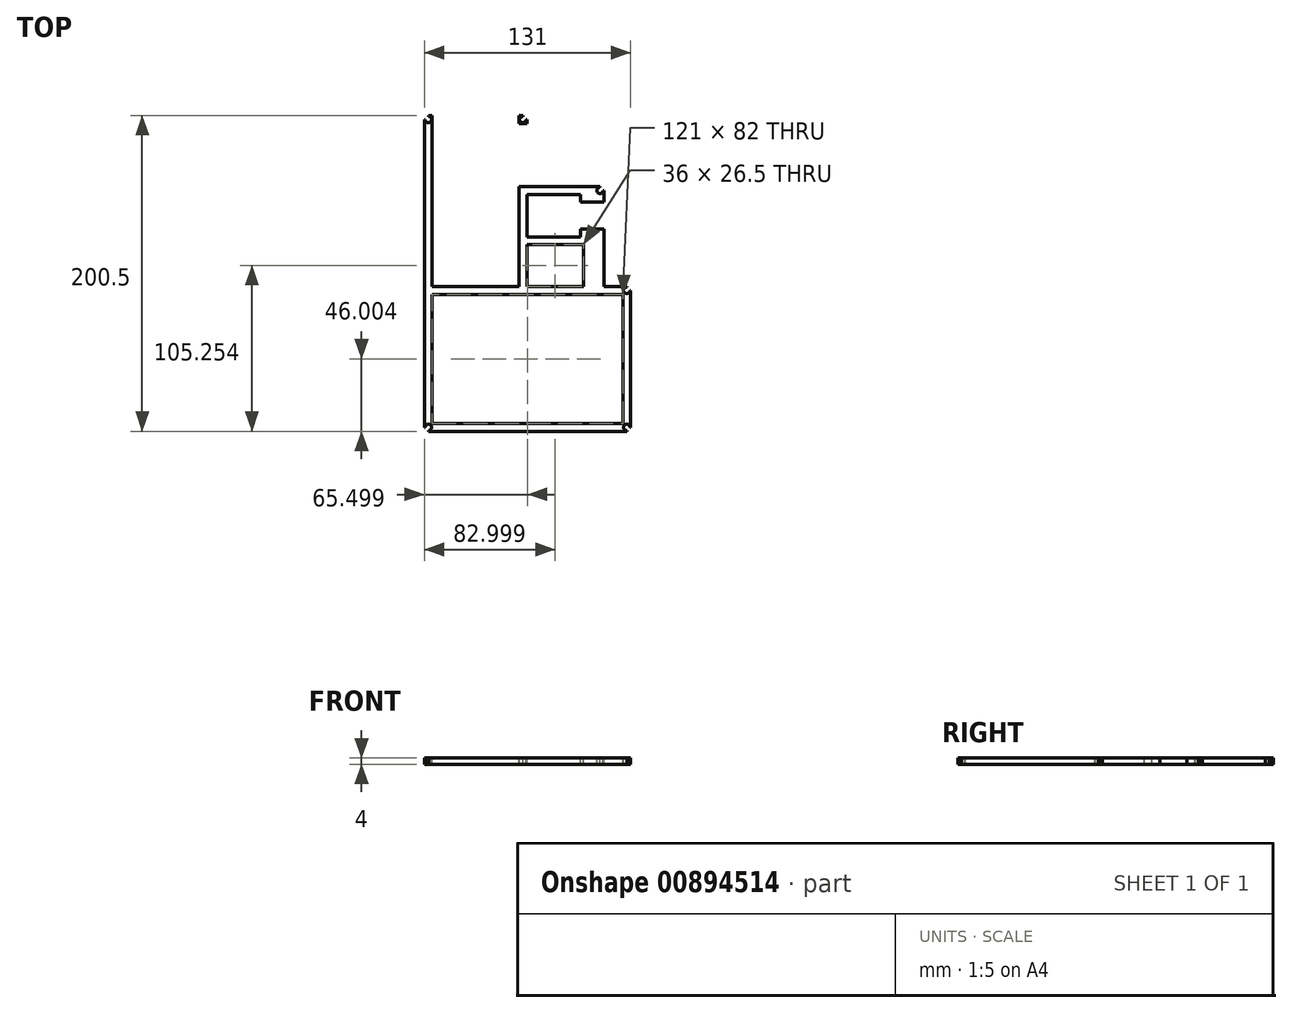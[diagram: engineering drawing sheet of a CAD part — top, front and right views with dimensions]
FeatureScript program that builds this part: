
annotation { "Feature Type Name" : "Feature", "Feature Type Description" : "" }
export const myFeature = defineFeature(function(context is Context, id is Id, definition is map)
    precondition{}
    {
        {
            var Q0;
            Q0=qCreatedBy(makeId("Top.planeOp"),FACE);
            var sketch = newSketch(context, id + "F0", { "sketchPlane" : qUnion([Q0])});
            skLineSegment(sketch, "E0.bottom", {"start": v(-40.7, -58.83) * mm, "end": v(14.3, -58.83) * mm});
            skLineSegment(sketch, "E0.top", {"start": v(-40.7, 44.67) * mm, "end": v(14.3, 44.67) * mm});
            skLineSegment(sketch, "E0.left", {"start": v(-40.7, -58.83) * mm, "end": v(-40.7, 44.67) * mm});
            skLineSegment(sketch, "E0.right", {"start": v(14.3, -58.83) * mm, "end": v(14.3, 44.67) * mm});
            skLineSegment(sketch, "E1.bottom", {"start": v(-45.7, 49.67) * mm, "end": v(85.3, 49.67) * mm});
            skLineSegment(sketch, "E1.top", {"start": v(-45.7, -150.83) * mm, "end": v(85.3, -150.83) * mm});
            skLineSegment(sketch, "E1.left", {"start": v(-45.7, 49.67) * mm, "end": v(-45.7, -150.83) * mm});
            skLineSegment(sketch, "E1.right", {"start": v(85.3, 49.67) * mm, "end": v(85.3, -150.83) * mm});
            skLineSegment(sketch, "E2.bottom", {"start": v(-40.7, -63.83) * mm, "end": v(80.3, -63.83) * mm});
            skLineSegment(sketch, "E2.top", {"start": v(-40.7, -145.83) * mm, "end": v(80.3, -145.83) * mm});
            skLineSegment(sketch, "E2.left", {"start": v(-40.7, -63.83) * mm, "end": v(-40.7, -145.83) * mm});
            skLineSegment(sketch, "E2.right", {"start": v(80.3, -63.83) * mm, "end": v(80.3, -145.83) * mm});
            skLineSegment(sketch, "E3.top", {"start": v(14.3, -63.83) * mm, "end": v(19.3, -63.83) * mm});
            skLineSegment(sketch, "E4.bottom", {"start": v(19.3, -58.83) * mm, "end": v(55.3, -58.83) * mm});
            skLineSegment(sketch, "E4.top", {"start": v(19.3, -32.33) * mm, "end": v(55.3, -32.33) * mm});
            skLineSegment(sketch, "E4.left", {"start": v(19.3, -58.83) * mm, "end": v(19.3, -32.33) * mm});
            skLineSegment(sketch, "E4.right", {"start": v(55.3, -58.83) * mm, "end": v(55.3, -32.33) * mm});
            skLineSegment(sketch, "E5.right", {"start": v(14.3, -32.33) * mm, "end": v(14.3, -27.33) * mm});
            skLineSegment(sketch, "E6.bottom", {"start": v(19.3, -27.33) * mm, "end": v(53.3, -27.33) * mm});
            skLineSegment(sketch, "E6.top", {"start": v(19.3, -0.33) * mm, "end": v(53.3, -0.33) * mm});
            skLineSegment(sketch, "E6.left", {"start": v(19.3, -27.33) * mm, "end": v(19.3, -0.33) * mm});
            skLineSegment(sketch, "E6.right", {"start": v(53.3, -27.33) * mm, "end": v(53.3, -0.33) * mm});
            skLineSegment(sketch, "E7", {"start": v(53.3, -27.33) * mm, "end": v(53.3, -22.33) * mm});
            skLineSegment(sketch, "E8", {"start": v(53.3, -22.33) * mm, "end": v(53.3, -5.33) * mm});
            skLineSegment(sketch, "E9.bottom", {"start": v(53.3, -5.33) * mm, "end": v(53.3, -5.33) * mm});
            skLineSegment(sketch, "E9.top", {"start": v(53.3, -22.33) * mm, "end": v(53.3, -22.33) * mm});
            skLineSegment(sketch, "E9.left", {"start": v(53.3, -5.33) * mm, "end": v(53.3, -22.33) * mm});
            skLineSegment(sketch, "E9.right", {"start": v(53.3, -5.33) * mm, "end": v(53.3, -22.33) * mm});
            skLineSegment(sketch, "E10.bottom", {"start": v(53.3, -22.33) * mm, "end": v(63.3, -22.33) * mm});
            skLineSegment(sketch, "E10.top", {"start": v(53.3, -5.33) * mm, "end": v(63.3, -5.33) * mm});
            skLineSegment(sketch, "E10.right", {"start": v(63.3, -22.33) * mm, "end": v(63.3, -5.33) * mm});
            skLineSegment(sketch, "E11.bottom", {"start": v(14.3, 44.67) * mm, "end": v(19.3, 44.67) * mm});
            skLineSegment(sketch, "E11.top", {"start": v(14.3, 49.67) * mm, "end": v(19.3, 49.67) * mm});
            skLineSegment(sketch, "E11.left", {"start": v(14.3, 44.67) * mm, "end": v(14.3, 49.67) * mm});
            skLineSegment(sketch, "E11.right", {"start": v(19.3, 44.67) * mm, "end": v(19.3, 49.67) * mm});
            skLineSegment(sketch, "E12.bottom", {"start": v(19.3, -0.33) * mm, "end": v(14.3, -0.33) * mm});
            skLineSegment(sketch, "E12.top", {"start": v(19.3, 4.67) * mm, "end": v(14.3, 4.67) * mm});
            skLineSegment(sketch, "E12.left", {"start": v(19.3, -0.33) * mm, "end": v(19.3, 4.67) * mm});
            skLineSegment(sketch, "E12.right", {"start": v(14.3, -0.33) * mm, "end": v(14.3, 4.67) * mm});
            skLineSegment(sketch, "E13.bottom", {"start": v(85.3, 49.67) * mm, "end": v(80.3, 49.67) * mm});
            skLineSegment(sketch, "E13.left", {"start": v(85.3, 49.67) * mm, "end": v(85.3, 44.67) * mm});
            skLineSegment(sketch, "E14.top", {"start": v(19.3, 49.67) * mm, "end": v(85.3, 49.67) * mm});
            skLineSegment(sketch, "E14.left", {"start": v(19.3, 4.67) * mm, "end": v(19.3, 49.67) * mm});
            skLineSegment(sketch, "E14.right", {"start": v(85.3, 4.67) * mm, "end": v(85.3, 49.67) * mm});
            skLineSegment(sketch, "E15.bottom", {"start": v(80.3, -63.83) * mm, "end": v(85.3, -63.83) * mm});
            skLineSegment(sketch, "E15.top", {"start": v(80.3, -58.83) * mm, "end": v(85.3, -58.83) * mm});
            skLineSegment(sketch, "E15.left", {"start": v(80.3, -63.83) * mm, "end": v(80.3, -58.83) * mm});
            skLineSegment(sketch, "E15.right", {"start": v(85.3, -63.83) * mm, "end": v(85.3, -58.83) * mm});
            skLineSegment(sketch, "E16", {"start": v(63.3, -5.33) * mm, "end": v(68.3, -5.33) * mm});
            skLineSegment(sketch, "E17", {"start": v(68.3, -5.33) * mm, "end": v(68.3, -22.33) * mm});
            skLineSegment(sketch, "E18.bottom", {"start": v(85.3, -58.83) * mm, "end": v(68.3, -58.83) * mm});
            skLineSegment(sketch, "E18.left", {"start": v(85.3, -58.83) * mm, "end": v(85.3, 4.67) * mm});
            skLineSegment(sketch, "E18.right", {"start": v(68.3, -58.83) * mm, "end": v(68.3, 4.67) * mm});
            skLineSegment(sketch, "E19", {"start": v(19.3, 4.67) * mm, "end": v(68.3, 4.67) * mm});
            skLineSegment(sketch, "E20.bottom", {"start": v(68.3, 4.67) * mm, "end": v(65.8, 4.67) * mm});
            skLineSegment(sketch, "E20.top", {"start": v(68.3, 2.17) * mm, "end": v(65.8, 2.17) * mm});
            skLineSegment(sketch, "E20.left", {"start": v(68.3, 4.67) * mm, "end": v(68.3, 2.17) * mm});
            skLineSegment(sketch, "E20.right", {"start": v(65.8, 4.67) * mm, "end": v(65.8, 2.17) * mm});
            skLineSegment(sketch, "E21.bottom", {"start": v(19.3, 44.67) * mm, "end": v(16.8, 44.67) * mm});
            skLineSegment(sketch, "E21.top", {"start": v(19.3, 47.17) * mm, "end": v(16.8, 47.17) * mm});
            skLineSegment(sketch, "E21.left", {"start": v(19.3, 44.67) * mm, "end": v(19.3, 47.17) * mm});
            skLineSegment(sketch, "E22.bottom", {"start": v(85.3, -58.83) * mm, "end": v(82.8, -58.83) * mm});
            skLineSegment(sketch, "E22.top", {"start": v(85.3, -61.33) * mm, "end": v(82.8, -61.33) * mm});
            skLineSegment(sketch, "E22.left", {"start": v(85.3, -58.83) * mm, "end": v(85.3, -61.33) * mm});
            skLineSegment(sketch, "E22.right", {"start": v(82.8, -58.83) * mm, "end": v(82.8, -61.33) * mm});
            skLineSegment(sketch, "E23.bottom", {"start": v(85.3, -150.83) * mm, "end": v(82.8, -150.83) * mm});
            skLineSegment(sketch, "E23.top", {"start": v(85.3, -148.33) * mm, "end": v(82.8, -148.33) * mm});
            skLineSegment(sketch, "E23.left", {"start": v(85.3, -150.83) * mm, "end": v(85.3, -148.33) * mm});
            skLineSegment(sketch, "E23.right", {"start": v(82.8, -150.83) * mm, "end": v(82.8, -148.33) * mm});
            skLineSegment(sketch, "E24.bottom", {"start": v(-45.7, -150.83) * mm, "end": v(-43.2, -150.83) * mm});
            skLineSegment(sketch, "E24.top", {"start": v(-45.7, -148.33) * mm, "end": v(-43.2, -148.33) * mm});
            skLineSegment(sketch, "E24.left", {"start": v(-45.7, -150.83) * mm, "end": v(-45.7, -148.33) * mm});
            skLineSegment(sketch, "E24.right", {"start": v(-43.2, -150.83) * mm, "end": v(-43.2, -148.33) * mm});
            skLineSegment(sketch, "E25.bottom", {"start": v(-45.7, 49.67) * mm, "end": v(-43.2, 49.67) * mm});
            skLineSegment(sketch, "E25.top", {"start": v(-45.7, 47.17) * mm, "end": v(-43.2, 47.17) * mm});
            skLineSegment(sketch, "E25.left", {"start": v(-45.7, 49.67) * mm, "end": v(-45.7, 47.17) * mm});
            skLineSegment(sketch, "E25.right", {"start": v(-43.2, 49.67) * mm, "end": v(-43.2, 47.17) * mm});
            skLineSegment(sketch, "E26.bottom", {"start": v(19.3, 49.67) * mm, "end": v(16.8, 49.67) * mm});
            skLineSegment(sketch, "E26.left", {"start": v(19.3, 49.67) * mm, "end": v(19.3, 47.17) * mm});
            skLineSegment(sketch, "E26.right", {"start": v(16.8, 49.67) * mm, "end": v(16.8, 47.17) * mm});
            skCircle(sketch, "E27", {"center": v(16.8, 47.17) * mm, "radius": 2 * mm});
            skCircle(sketch, "E28", {"center": v(65.8, 2.17) * mm, "radius": 2 * mm});
            skCircle(sketch, "E29", {"center": v(82.8, -61.33) * mm, "radius": 2 * mm});
            skCircle(sketch, "E30", {"center": v(82.8, -148.33) * mm, "radius": 2 * mm});
            skCircle(sketch, "E31", {"center": v(-43.2, -148.33) * mm, "radius": 2 * mm});
            skCircle(sketch, "E32", {"center": v(-43.2, 47.17) * mm, "radius": 2 * mm});
            skLineSegment(sketch, "E33.bottom", {"start": v(-40.7, -63.83) * mm, "end": v(-37.3, -63.83) * mm});
            skLineSegment(sketch, "E33.top", {"start": v(-40.7, -67.23) * mm, "end": v(-37.3, -67.23) * mm});
            skLineSegment(sketch, "E33.left", {"start": v(-40.7, -63.83) * mm, "end": v(-40.7, -67.23) * mm});
            skLineSegment(sketch, "E33.right", {"start": v(-37.3, -63.83) * mm, "end": v(-37.3, -67.23) * mm});
            skLineSegment(sketch, "E34.bottom", {"start": v(-40.7, -145.83) * mm, "end": v(-37.3, -145.83) * mm});
            skLineSegment(sketch, "E34.top", {"start": v(-40.7, -142.43) * mm, "end": v(-37.3, -142.43) * mm});
            skLineSegment(sketch, "E34.left", {"start": v(-40.7, -145.83) * mm, "end": v(-40.7, -142.43) * mm});
            skLineSegment(sketch, "E34.right", {"start": v(-37.3, -145.83) * mm, "end": v(-37.3, -142.43) * mm});
            skLineSegment(sketch, "E35.bottom", {"start": v(80.3, -145.83) * mm, "end": v(76.9, -145.83) * mm});
            skLineSegment(sketch, "E35.top", {"start": v(80.3, -142.43) * mm, "end": v(76.9, -142.43) * mm});
            skLineSegment(sketch, "E35.left", {"start": v(80.3, -145.83) * mm, "end": v(80.3, -142.43) * mm});
            skLineSegment(sketch, "E35.right", {"start": v(76.9, -145.83) * mm, "end": v(76.9, -142.43) * mm});
            skLineSegment(sketch, "E36.bottom", {"start": v(80.3, -63.83) * mm, "end": v(76.9, -63.83) * mm});
            skLineSegment(sketch, "E36.top", {"start": v(80.3, -67.23) * mm, "end": v(76.9, -67.23) * mm});
            skLineSegment(sketch, "E36.left", {"start": v(80.3, -63.83) * mm, "end": v(80.3, -67.23) * mm});
            skLineSegment(sketch, "E36.right", {"start": v(76.9, -63.83) * mm, "end": v(76.9, -67.23) * mm});
            skLineSegment(sketch, "E37.bottom", {"start": v(-40.7, -58.83) * mm, "end": v(-37.7, -58.83) * mm});
            skLineSegment(sketch, "E37.top", {"start": v(-40.7, 28.47) * mm, "end": v(-37.7, 28.47) * mm});
            skLineSegment(sketch, "E37.left", {"start": v(-40.7, -58.83) * mm, "end": v(-40.7, 28.47) * mm});
            skLineSegment(sketch, "E37.right", {"start": v(-37.7, -58.83) * mm, "end": v(-37.7, 28.47) * mm});
            skLineSegment(sketch, "E38.bottom", {"start": v(-37.7, -58.83) * mm, "end": v(-40.7, -58.83) * mm});
            skLineSegment(sketch, "E38.top", {"start": v(-37.7, -52.83) * mm, "end": v(-40.7, -52.83) * mm});
            skLineSegment(sketch, "E38.left", {"start": v(-37.7, -58.83) * mm, "end": v(-37.7, -52.83) * mm});
            skLineSegment(sketch, "E38.right", {"start": v(-40.7, -58.83) * mm, "end": v(-40.7, -52.83) * mm});
            skLineSegment(sketch, "E39.bottom", {"start": v(14.3, -58.83) * mm, "end": v(11.3, -58.83) * mm});
            skLineSegment(sketch, "E39.top", {"start": v(14.3, 29.87) * mm, "end": v(11.3, 29.87) * mm});
            skLineSegment(sketch, "E39.left", {"start": v(14.3, -58.83) * mm, "end": v(14.3, 29.87) * mm});
            skLineSegment(sketch, "E39.right", {"start": v(11.3, -58.83) * mm, "end": v(11.3, 29.87) * mm});
            skLineSegment(sketch, "E40.top", {"start": v(14.3, -47.23) * mm, "end": v(11.3, -47.23) * mm});
            skLineSegment(sketch, "E40.left", {"start": v(14.3, -58.83) * mm, "end": v(14.3, -47.23) * mm});
            skLineSegment(sketch, "E40.right", {"start": v(11.3, -58.83) * mm, "end": v(11.3, -47.23) * mm});
            skCircle(sketch, "E41", {"center": v(-37.7, -52.83) * mm, "radius": 2 * mm});
            skCircle(sketch, "E42", {"center": v(-37.7, 28.47) * mm, "radius": 2 * mm});
            skCircle(sketch, "E43", {"center": v(11.3, 29.87) * mm, "radius": 2 * mm});
            skCircle(sketch, "E44", {"center": v(11.3, -47.23) * mm, "radius": 2 * mm});
            skLineSegment(sketch, "E45.bottom", {"start": v(19.3, -0.33) * mm, "end": v(28.55, -0.33) * mm});
            skLineSegment(sketch, "E45.top", {"start": v(19.3, -2.28) * mm, "end": v(28.55, -2.28) * mm});
            skLineSegment(sketch, "E45.left", {"start": v(19.3, -0.33) * mm, "end": v(19.3, -2.28) * mm});
            skLineSegment(sketch, "E45.right", {"start": v(28.55, -0.33) * mm, "end": v(28.55, -2.28) * mm});
            skLineSegment(sketch, "E46.bottom", {"start": v(19.3, -27.33) * mm, "end": v(28.55, -27.33) * mm});
            skLineSegment(sketch, "E46.top", {"start": v(19.3, -25.38) * mm, "end": v(28.55, -25.38) * mm});
            skLineSegment(sketch, "E46.left", {"start": v(19.3, -27.33) * mm, "end": v(19.3, -25.38) * mm});
            skLineSegment(sketch, "E46.right", {"start": v(28.55, -27.33) * mm, "end": v(28.55, -25.38) * mm});
            skLineSegment(sketch, "E47.bottom", {"start": v(53.3, -0.33) * mm, "end": v(51.35, -0.33) * mm});
            skLineSegment(sketch, "E47.top", {"start": v(53.3, -2.28) * mm, "end": v(51.35, -2.28) * mm});
            skLineSegment(sketch, "E47.left", {"start": v(53.3, -0.33) * mm, "end": v(53.3, -2.28) * mm});
            skLineSegment(sketch, "E47.right", {"start": v(51.35, -0.33) * mm, "end": v(51.35, -2.28) * mm});
            skLineSegment(sketch, "E48.bottom", {"start": v(53.3, -27.33) * mm, "end": v(51.35, -27.33) * mm});
            skLineSegment(sketch, "E48.top", {"start": v(53.3, -25.38) * mm, "end": v(51.35, -25.38) * mm});
            skLineSegment(sketch, "E48.left", {"start": v(53.3, -27.33) * mm, "end": v(53.3, -25.38) * mm});
            skLineSegment(sketch, "E48.right", {"start": v(51.35, -27.33) * mm, "end": v(51.35, -25.38) * mm});
            skLineSegment(sketch, "E49.bottom", {"start": v(55.3, -32.33) * mm, "end": v(53.6, -32.33) * mm});
            skLineSegment(sketch, "E49.top", {"start": v(55.3, -34.03) * mm, "end": v(53.6, -34.03) * mm});
            skLineSegment(sketch, "E49.left", {"start": v(55.3, -32.33) * mm, "end": v(55.3, -34.03) * mm});
            skLineSegment(sketch, "E49.right", {"start": v(53.6, -32.33) * mm, "end": v(53.6, -34.03) * mm});
            skLineSegment(sketch, "E50.bottom", {"start": v(55.3, -58.83) * mm, "end": v(53.6, -58.83) * mm});
            skLineSegment(sketch, "E50.top", {"start": v(55.3, -57.13) * mm, "end": v(53.6, -57.13) * mm});
            skLineSegment(sketch, "E50.left", {"start": v(55.3, -58.83) * mm, "end": v(55.3, -57.13) * mm});
            skLineSegment(sketch, "E50.right", {"start": v(53.6, -58.83) * mm, "end": v(53.6, -57.13) * mm});
            skCircle(sketch, "E51", {"center": v(53.6, -34.03) * mm, "radius": 1.2 * mm});
            skCircle(sketch, "E52", {"center": v(53.6, -57.13) * mm, "radius": 1.2 * mm});
            skCircle(sketch, "E53", {"center": v(51.35, -25.38) * mm, "radius": 1.15 * mm});
            skCircle(sketch, "E54", {"center": v(28.55, -25.38) * mm, "radius": 1.15 * mm});
            skCircle(sketch, "E55", {"center": v(28.55, -2.28) * mm, "radius": 1.15 * mm});
            skCircle(sketch, "E56", {"center": v(51.35, -2.28) * mm, "radius": 1.15 * mm});
            skCircle(sketch, "E57", {"center": v(-37.3, -67.23) * mm, "radius": 1.4 * mm});
            skCircle(sketch, "E58", {"center": v(76.9, -67.23) * mm, "radius": 1.4 * mm});
            skCircle(sketch, "E59", {"center": v(-37.3, -142.43) * mm, "radius": 1.4 * mm});
            skCircle(sketch, "E60", {"center": v(76.9, -142.43) * mm, "radius": 1.4 * mm});
            skLineSegment(sketch, "E61", {"start": v(68.3, -22.33) * mm, "end": v(63.3, -22.33) * mm});
            skLineSegment(sketch, "E62.bottom", {"start": v(-40.7, 44.67) * mm, "end": v(-35.7, 44.67) * mm});
            skLineSegment(sketch, "E62.top", {"start": v(-40.7, 49.67) * mm, "end": v(-35.7, 49.67) * mm});
            skLineSegment(sketch, "E62.left", {"start": v(-40.7, 44.67) * mm, "end": v(-40.7, 49.67) * mm});
            skLineSegment(sketch, "E62.right", {"start": v(-35.7, 44.67) * mm, "end": v(-35.7, 49.67) * mm});
            skLineSegment(sketch, "E63.bottom", {"start": v(14.3, 44.67) * mm, "end": v(9.3, 44.67) * mm});
            skLineSegment(sketch, "E63.top", {"start": v(14.3, 49.67) * mm, "end": v(9.3, 49.67) * mm});
            skLineSegment(sketch, "E63.right", {"start": v(9.3, 44.67) * mm, "end": v(9.3, 49.67) * mm});
            skSolve(sketch);
        }
        {
            var Q0;
            {var subQ1=sQuery(id+"F0.wireOp",EDGE,"E23.bottom");Q0=makeQuery(id+"F0.imprint","IMPRINT",FACE,{"disambiguationData":[TD([[makeQuery(id+"F0.imprint","IMPRINT",EDGE,{"derivedFrom":subQ1}),-1.0]])]});}
            var Q1;
            {var subQ1=sQuery(id+"F0.wireOp",EDGE,"E24.bottom");Q1=makeQuery(id+"F0.imprint","IMPRINT",FACE,{"disambiguationData":[TD([[makeQuery(id+"F0.imprint","IMPRINT",EDGE,{"derivedFrom":subQ1}),1.0]])]});}
            var Q2;
            {var subQ1=sQuery(id+"F0.wireOp",EDGE,"E25.bottom");Q2=makeQuery(id+"F0.imprint","IMPRINT",FACE,{"disambiguationData":[TD([[makeQuery(id+"F0.imprint","IMPRINT",EDGE,{"derivedFrom":subQ1}),-1.0]])]});}
            var Q3;
            {var subQ1=sQuery(id+"F0.wireOp",EDGE,"E22.bottom");Q3=makeQuery(id+"F0.imprint","IMPRINT",FACE,{"disambiguationData":[TD([[makeQuery(id+"F0.imprint","IMPRINT",EDGE,{"derivedFrom":subQ1}),1.0]])]});}
            var Q4;
            {var subQ1=sQuery(id+"F0.wireOp",EDGE,"E26.bottom");Q4=makeQuery(id+"F0.imprint","IMPRINT",FACE,{"disambiguationData":[TD([[makeQuery(id+"F0.imprint","IMPRINT",EDGE,{"derivedFrom":subQ1}),1.0]])]});}
            var Q5;
            Q5=makeQuery(id+"F0.imprint","IMPRINT",FACE,{"disambiguationData":[TD([[makeQuery(id+"F0.imprint","IMPRINT",EDGE,{"derivedFrom":sQuery(id+"F0.wireOp",EDGE,"E15.bottom")}),1.0]])]});
            var Q6;
            Q6=makeQuery(id+"F0.imprint","IMPRINT",FACE,{"disambiguationData":[TD([[makeQuery(id+"F0.imprint","IMPRINT",EDGE,{"derivedFrom":sQuery(id+"F0.wireOp",EDGE,"E11.bottom")}),1.0]])]});
            var Q7;
            Q7=makeQuery(id+"F0.imprint","IMPRINT",FACE,{"disambiguationData":[TD([[makeQuery(id+"F0.imprint","IMPRINT",EDGE,{"derivedFrom":sQuery(id+"F0.wireOp",EDGE,"E0.bottom")}),-1.0]])]});
            var Q8;
            {var subQ0=sQuery(id+"F0.wireOp",EDGE,"E12.bottom");Q8=makeQuery(id+"F0.imprint","IMPRINT",FACE,{"disambiguationData":[TD([[makeQuery(id+"F0.imprint","IMPRINT",EDGE,{"derivedFrom":subQ0}),-1.0]])]});}
            var Q9;
            {var subQ1=sQuery(id+"F0.wireOp",EDGE,"E0.right");Q9=makeQuery(id+"F0.imprint","IMPRINT",FACE,{"disambiguationData":[TD([[makeQuery(id+"F0.imprint","IMPRINT",EDGE,{"derivedFrom":subQ1}),-1.0]])]});}
            var Q10;
            Q10=makeQuery(id+"F0.imprint","IMPRINT",FACE,{"disambiguationData":[TD([[makeQuery(id+"F0.imprint","IMPRINT",EDGE,{"derivedFrom":sQuery(id+"F0.wireOp",EDGE,"E6.top")}),1.0]])]});
            var Q11;
            {var subQ1=sQuery(id+"F0.wireOp",EDGE,"E20.bottom");Q11=makeQuery(id+"F0.imprint","IMPRINT",FACE,{"disambiguationData":[TD([[makeQuery(id+"F0.imprint","IMPRINT",EDGE,{"derivedFrom":subQ1}),1.0]])]});}
            var Q12;
            Q12=makeQuery(id+"F0.imprint","IMPRINT",FACE,{"disambiguationData":[TD([[makeQuery(id+"F0.imprint","IMPRINT",EDGE,{"derivedFrom":sQuery(id+"F0.wireOp",EDGE,"E62.bottom")}),1.0]])]});
            var Q13;
            Q13=makeQuery(id+"F0.imprint","IMPRINT",FACE,{"disambiguationData":[TD([[makeQuery(id+"F0.imprint","IMPRINT",EDGE,{"derivedFrom":sQuery(id+"F0.wireOp",EDGE,"E63.bottom")}),-1.0]])]});
            extrude(context, id + "F1", {"entities" : qUnion([Q0, Q1, Q2, Q3, Q4, Q5, Q6, Q7, Q8, Q9, Q10, Q11, Q12, Q13]), "oppositeDirection" : true, "depth" : 4 * mm, "offsetDistance" : 25 * mm});
        }
    });
